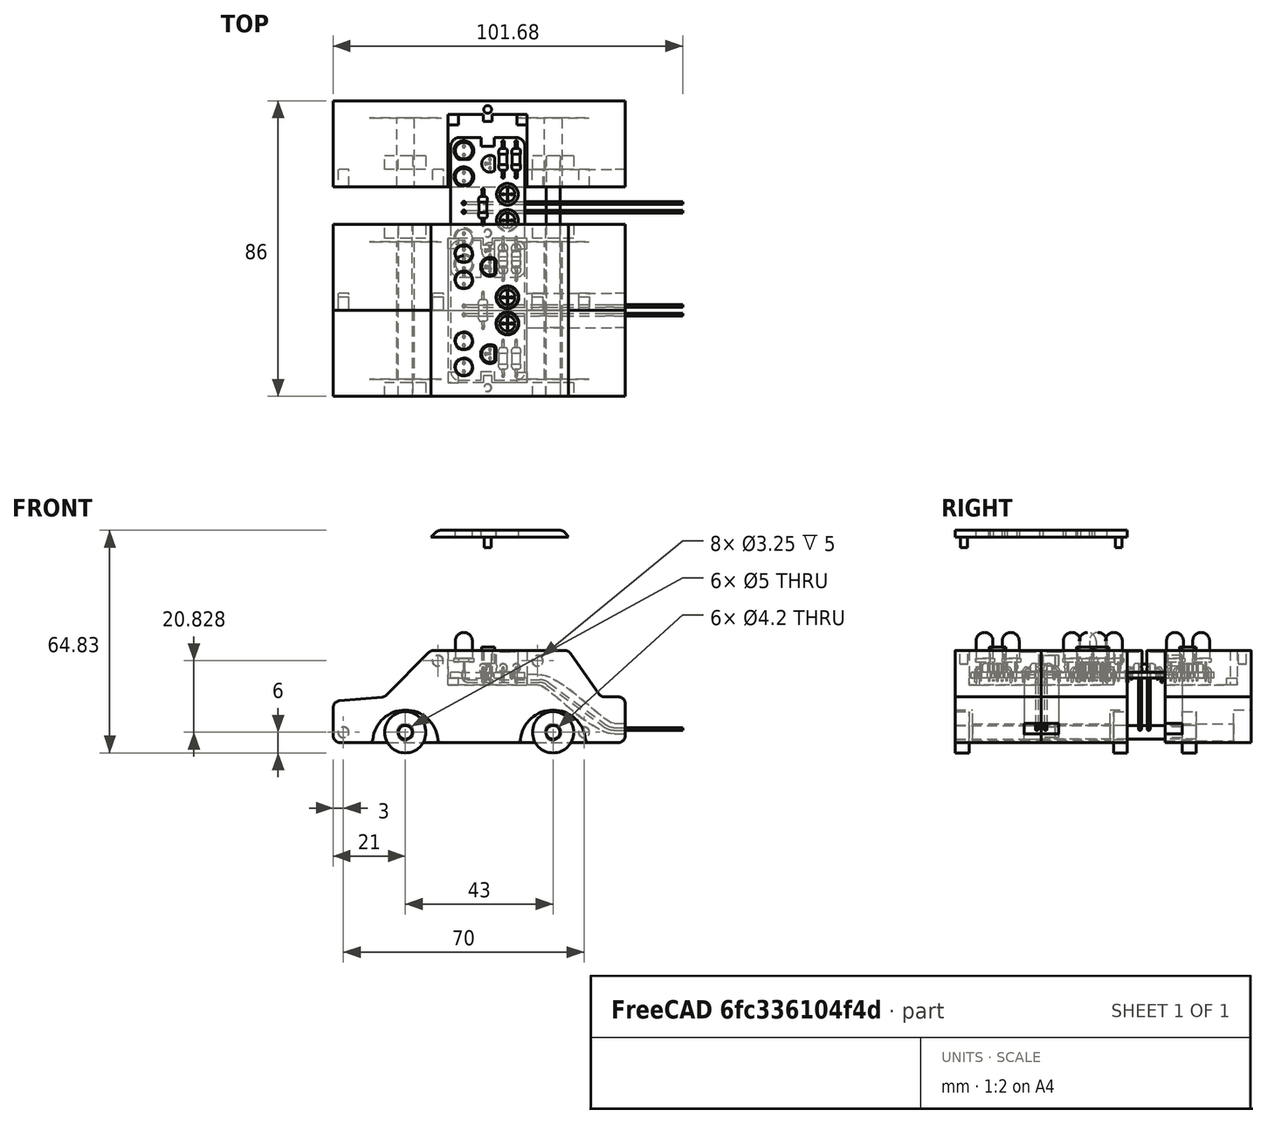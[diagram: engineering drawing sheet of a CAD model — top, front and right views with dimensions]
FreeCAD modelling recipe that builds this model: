
FCSTD DOCUMENT  (FreeCAD 0.21R30029 (Git))
Label: Assembly
License: All rights reserved
LicenseURL: http://en.wikipedia.org/wiki/All_rights_reserved
objects: PartDesign::FeatureBase×26, PartDesign::Body×26, TechDraw::DrawViewPart×13, Part::FeaturePython×10, App::DocumentObjectGroup×6, App::Part×2, TechDraw::DrawSVGTemplate×1, TechDraw::DrawPage×1
note: 62 computed .brp shape members not serialized (recipe doc carries the construction recipe); baked Part::Feature solids carry a one-line shape summary decoded from their .brp

FEATURE [Part::FeaturePython] b_PCB1_001_  label="PCB1_001"  # a2plus imported part (geometry in sourceFile) (typed FeaturePython)
  Placement = pos=(45.5,-0.49,18.8275) rot=(0,0,1;1.5708rad)
  a2p_Version = V0.1
  fixedPosition = true
  objectType = a2pPart
  sourceFile = PCB_w_Wire.FCStd
  subassemblyImport = false
  timeLastImport = 1.66233e+09
  updateColors = true
FEATURE [Part::FeaturePython] b_LightTop_001_  label="LightTop_001"  # a2plus imported part (geometry in sourceFile) (typed FeaturePython)
  Placement = pos=(28.46,0,26.83) rot=(0,0,1;0rad)
  a2p_Version = V0.1
  fixedPosition = false
  objectType = a2pPart
  sourceFile = ./LightTop.FCStd
  subassemblyImport = false
  timeLastImport = 1.66241e+09
  updateColors = true
FEATURE [Part::FeaturePython] b_Car_001_  label="Car_Body001_001"  # a2plus imported part (geometry in sourceFile) (typed FeaturePython)
  a2p_Version = V0.1
  fixedPosition = false
  objectType = a2pPart
  sourceFile = ./Car.FCStd
  sourcePart = Body001
  subassemblyImport = false
  timeLastImport = 1.66233e+09
  updateColors = true
FEATURE [Part::FeaturePython] b_Car_001_001  label="Car_Body002_001"  # a2plus imported part (geometry in sourceFile) (typed FeaturePython)
  a2p_Version = V0.1
  fixedPosition = false
  objectType = a2pPart
  sourceFile = ./Car.FCStd
  sourcePart = Body002
  subassemblyImport = false
  timeLastImport = 1.66233e+09
  updateColors = true
FEATURE [Part::FeaturePython] b_Car_001_002  label="Car_Body003_001"  # a2plus imported part (geometry in sourceFile) (typed FeaturePython)
  a2p_Version = V0.1
  fixedPosition = false
  objectType = a2pPart
  sourceFile = ./Car.FCStd
  sourcePart = Body003
  subassemblyImport = false
  timeLastImport = 1.66233e+09
  updateColors = true
FEATURE [Part::FeaturePython] b_Car_001_003  label="Car_Body004_001"  # a2plus imported part (geometry in sourceFile) (typed FeaturePython)
  a2p_Version = V0.1
  fixedPosition = false
  objectType = a2pPart
  sourceFile = ./Car.FCStd
  sourcePart = Body004
  subassemblyImport = false
  timeLastImport = 1.66233e+09
  updateColors = true
FEATURE [Part::FeaturePython] b_Car_Body002_001_  label="Car_Body002_002"  # a2plus imported part (geometry in sourceFile) (typed FeaturePython)
  Placement = pos=(0,46,0) rot=(0,0,1;0rad)
  a2p_Version = V0.1
  fixedPosition = false
  objectType = a2pPart
  sourceFile = ./Car.FCStd
  sourcePart = Body002
  subassemblyImport = false
  timeLastImport = 1.66233e+09
  updateColors = true
FEATURE [Part::FeaturePython] b_Car_Body002_001_001  label="Car_Body002_003"  # a2plus imported part (geometry in sourceFile) (typed FeaturePython)
  Placement = pos=(43,46,0) rot=(0,0,1;0rad)
  a2p_Version = V0.1
  fixedPosition = false
  objectType = a2pPart
  sourceFile = ./Car.FCStd
  sourcePart = Body002
  subassemblyImport = false
  timeLastImport = 1.66233e+09
  updateColors = true
FEATURE [Part::FeaturePython] b_Car_Body002_001_002  label="Car_Body002_004"  # a2plus imported part (geometry in sourceFile) (typed FeaturePython)
  Placement = pos=(43,0,0) rot=(0,0,1;0rad)
  a2p_Version = V0.1
  fixedPosition = false
  objectType = a2pPart
  sourceFile = ./Car.FCStd
  sourcePart = Body002
  subassemblyImport = false
  timeLastImport = 1.66233e+09
  updateColors = true
FEATURE [Part::FeaturePython] b_Car_Body001_001_  label="Car_Body001_002"  # a2plus imported part (geometry in sourceFile) (typed FeaturePython)
  Placement = pos=(43,0,0) rot=(0,0,1;0rad)
  a2p_Version = V0.1
  fixedPosition = false
  objectType = a2pPart
  sourceFile = ./Car.FCStd
  sourcePart = Body001
  subassemblyImport = false
  timeLastImport = 1.66233e+09
  updateColors = true
FEATURE [App::DocumentObjectGroup] Group  label="Full Assembly"
  Group = -> [b_Car_Body001_001_,b_Car_Body002_001_002,b_Car_001_003,b_Car_Body002_001_001,b_Car_001_002,b_Car_001_001,b_Car_001_,b_LightTop_001_,b_Car_Body002_001_,b_PCB1_001_]
FEATURE [PartDesign::FeatureBase] Clone
  BaseFeature = -> b_Car_001_003
FEATURE [PartDesign::Body] Body
  BaseFeature = -> b_Car_001_003
  Group = -> [Clone]
  Origin = -> Origin
  Tip = -> Clone
FEATURE [PartDesign::FeatureBase] Clone001
  BaseFeature = -> b_PCB1_001_
  Placement = pos=(45.5,-0.49,18.8275) rot=(0,0,1;1.5708rad)
FEATURE [PartDesign::Body] Body001
  BaseFeature = -> b_PCB1_001_
  Group = -> [Clone001]
  Origin = -> Origin001
  Placement = pos=(0,30,0) rot=(0,0,1;0rad)
  Tip = -> Clone001
FEATURE [App::DocumentObjectGroup] Group001  label="Step 1"
  Group = -> [Body,Body001]
FEATURE [PartDesign::FeatureBase] Clone002
  BaseFeature = -> b_PCB1_001_
  Placement = pos=(45.5,-0.49,18.8275) rot=(0,0,1;1.5708rad)
FEATURE [PartDesign::Body] Body002
  BaseFeature = -> b_PCB1_001_
  Group = -> [Clone002]
  Origin = -> Origin002
  Tip = -> Clone002
FEATURE [PartDesign::FeatureBase] Clone003
  BaseFeature = -> b_Car_001_003
FEATURE [PartDesign::Body] Body003
  BaseFeature = -> b_Car_001_003
  Group = -> [Clone003]
  Origin = -> Origin003
  Tip = -> Clone003
FEATURE [PartDesign::FeatureBase] Clone004
  BaseFeature = -> b_Car_001_002
FEATURE [PartDesign::Body] Body004
  BaseFeature = -> b_Car_001_002
  Group = -> [Clone004]
  Origin = -> Origin004
  Placement = pos=(0,36,0) rot=(0,0,1;0rad)
  Tip = -> Clone004
FEATURE [App::DocumentObjectGroup] Group002  label="Step 2"
  Group = -> [Body002,Body003,Body004]
FEATURE [PartDesign::FeatureBase] Clone005
  BaseFeature = -> b_Car_Body002_001_002
  Placement = pos=(43,0,0) rot=(0,0,1;0rad)
FEATURE [PartDesign::Body] Body005
  BaseFeature = -> b_Car_Body002_001_002
  Group = -> [Clone005]
  Origin = -> Origin005
  Tip = -> Clone005
FEATURE [PartDesign::FeatureBase] Clone006
  BaseFeature = -> b_Car_Body001_001_
  Placement = pos=(43,0,0) rot=(0,0,1;0rad)
FEATURE [PartDesign::Body] Body006
  BaseFeature = -> b_Car_Body001_001_
  Group = -> [Clone006]
  Origin = -> Origin006
  Placement = pos=(0,20,0) rot=(0,0,1;0rad)
  Tip = -> Clone006
FEATURE [App::DocumentObjectGroup] Group003  label="Step 3"
  Group = -> [Body005,Body006]
FEATURE [PartDesign::FeatureBase] Clone007
  BaseFeature = -> b_Car_001_003
FEATURE [PartDesign::Body] Body007
  BaseFeature = -> b_Car_001_003
  Group = -> [Clone007]
  Origin = -> Origin007
  Tip = -> Clone007
FEATURE [PartDesign::FeatureBase] Clone008
  BaseFeature = -> b_Car_Body002_001_001
  Placement = pos=(43,46,0) rot=(0,0,1;0rad)
FEATURE [PartDesign::Body] Body008
  BaseFeature = -> b_Car_Body002_001_001
  Group = -> [Clone008]
  Origin = -> Origin008
  Placement = pos=(0,20,0) rot=(0,0,1;0rad)
  Tip = -> Clone008
FEATURE [PartDesign::FeatureBase] Clone009
  BaseFeature = -> b_Car_001_002
FEATURE [PartDesign::Body] Body009
  BaseFeature = -> b_Car_001_002
  Group = -> [Clone009]
  Origin = -> Origin009
  Tip = -> Clone009
FEATURE [PartDesign::FeatureBase] Clone010
  BaseFeature = -> b_Car_001_001
FEATURE [PartDesign::Body] Body010
  BaseFeature = -> b_Car_001_001
  Group = -> [Clone010]
  Origin = -> Origin010
  Tip = -> Clone010
FEATURE [PartDesign::FeatureBase] Clone011
  BaseFeature = -> b_Car_001_
FEATURE [PartDesign::Body] Body011
  BaseFeature = -> b_Car_001_
  Group = -> [Clone011]
  Origin = -> Origin011
  Tip = -> Clone011
FEATURE [PartDesign::FeatureBase] Clone012
  BaseFeature = -> b_PCB1_001_
  Placement = pos=(45.5,-0.49,18.8275) rot=(0,0,1;1.5708rad)
FEATURE [PartDesign::Body] Body012
  BaseFeature = -> b_PCB1_001_
  Group = -> [Clone012]
  Origin = -> Origin012
  Tip = -> Clone012
FEATURE [PartDesign::FeatureBase] Clone013
  BaseFeature = -> b_Car_Body002_001_
  Placement = pos=(0,46,0) rot=(0,0,1;0rad)
FEATURE [PartDesign::Body] Body013
  BaseFeature = -> b_Car_Body002_001_
  Group = -> [Clone013]
  Origin = -> Origin013
  Placement = pos=(0,20,0) rot=(0,0,1;0rad)
  Tip = -> Clone013
FEATURE [PartDesign::FeatureBase] Clone014
  BaseFeature = -> b_Car_Body001_001_
  Placement = pos=(43,0,0) rot=(0,0,1;0rad)
FEATURE [PartDesign::Body] Body014
  BaseFeature = -> b_Car_Body001_001_
  Group = -> [Clone014]
  Origin = -> Origin014
  Tip = -> Clone014
FEATURE [PartDesign::FeatureBase] Clone015
  BaseFeature = -> b_Car_Body002_001_002
  Placement = pos=(43,0,0) rot=(0,0,1;0rad)
FEATURE [PartDesign::Body] Body015
  BaseFeature = -> b_Car_Body002_001_002
  Group = -> [Clone015]
  Origin = -> Origin015
  Tip = -> Clone015
FEATURE [App::Part] Part
  Group = -> [Body014,Body015]
  Origin = -> Origin016
  Placement = pos=(0,-80,0) rot=(0,0,1;0rad)
FEATURE [App::Part] Part001
  Group = -> [Body010,Body011]
  Origin = -> Origin017
  Placement = pos=(0,-80,0) rot=(0,0,1;0rad)
FEATURE [App::DocumentObjectGroup] Group004  label="Step 4"
  Group = -> [Body007,Body008,Body009,Body012,Body013,Part,Part001]
FEATURE [PartDesign::FeatureBase] Clone016
  BaseFeature = -> b_Car_Body001_001_
  Placement = pos=(43,0,0) rot=(0,0,1;0rad)
FEATURE [PartDesign::Body] Body016
  BaseFeature = -> b_Car_Body001_001_
  Group = -> [Clone016]
  Origin = -> Origin018
  Tip = -> Clone016
FEATURE [PartDesign::FeatureBase] Clone017
  BaseFeature = -> b_Car_Body002_001_002
  Placement = pos=(43,0,0) rot=(0,0,1;0rad)
FEATURE [PartDesign::Body] Body017
  BaseFeature = -> b_Car_Body002_001_002
  Group = -> [Clone017]
  Origin = -> Origin019
  Tip = -> Clone017
FEATURE [PartDesign::FeatureBase] Clone018
  BaseFeature = -> b_Car_001_003
FEATURE [PartDesign::Body] Body018
  BaseFeature = -> b_Car_001_003
  Group = -> [Clone018]
  Origin = -> Origin020
  Tip = -> Clone018
FEATURE [PartDesign::FeatureBase] Clone019
  BaseFeature = -> b_Car_Body002_001_001
  Placement = pos=(43,46,0) rot=(0,0,1;0rad)
FEATURE [PartDesign::Body] Body019
  BaseFeature = -> b_Car_Body002_001_001
  Group = -> [Clone019]
  Origin = -> Origin021
  Tip = -> Clone019
FEATURE [PartDesign::FeatureBase] Clone020
  BaseFeature = -> b_Car_001_002
FEATURE [PartDesign::Body] Body020
  BaseFeature = -> b_Car_001_002
  Group = -> [Clone020]
  Origin = -> Origin022
  Tip = -> Clone020
FEATURE [PartDesign::FeatureBase] Clone021
  BaseFeature = -> b_Car_001_001
FEATURE [PartDesign::Body] Body021
  BaseFeature = -> b_Car_001_001
  Group = -> [Clone021]
  Origin = -> Origin023
  Tip = -> Clone021
FEATURE [PartDesign::FeatureBase] Clone022
  BaseFeature = -> b_Car_001_
FEATURE [PartDesign::Body] Body022
  BaseFeature = -> b_Car_001_
  Group = -> [Clone022]
  Origin = -> Origin024
  Tip = -> Clone022
FEATURE [PartDesign::FeatureBase] Clone023
  BaseFeature = -> b_LightTop_001_
  Placement = pos=(28.46,0,26.83) rot=(0,0,1;0rad)
FEATURE [PartDesign::Body] Body023
  BaseFeature = -> b_LightTop_001_
  Group = -> [Clone023]
  Origin = -> Origin025
  Placement = pos=(0,0,33) rot=(0,0,1;0rad)
  Tip = -> Clone023
FEATURE [PartDesign::FeatureBase] Clone024
  BaseFeature = -> b_Car_Body002_001_
  Placement = pos=(0,46,0) rot=(0,0,1;0rad)
FEATURE [PartDesign::Body] Body024
  BaseFeature = -> b_Car_Body002_001_
  Group = -> [Clone024]
  Origin = -> Origin026
  Tip = -> Clone024
FEATURE [PartDesign::FeatureBase] Clone025
  BaseFeature = -> b_PCB1_001_
  Placement = pos=(45.5,-0.49,18.8275) rot=(0,0,1;1.5708rad)
FEATURE [PartDesign::Body] Body025
  BaseFeature = -> b_PCB1_001_
  Group = -> [Clone025]
  Origin = -> Origin027
  Tip = -> Clone025
FEATURE [App::DocumentObjectGroup] Group005  label="Step 5"
  Group = -> [Body016,Body017,Body018,Body019,Body020,Body021,Body022,Body023,Body024,Body025]
FEATURE [TechDraw::DrawSVGTemplate] Template
  Height = 297
  Orientation = 1
  Width = 420
FEATURE [TechDraw::DrawViewPart] View
  CoarseView = false
  Direction = (0.577,0.577,0.577)
  Focus = 100
  HardHidden = false
  IsoCount = 0
  IsoHidden = false
  IsoVisible = false
  LockPosition = false
  Perspective = false
  Rotation = 0
  ScaleType = 0
  SeamHidden = false
  SeamVisible = true
  SmoothHidden = false
  SmoothVisible = true
  Source = -> [Group001]
  X = 51.7341
  XDirection = (-0.707,0.707,0)
  Y = 248.907
FEATURE [TechDraw::DrawViewPart] View001
  CoarseView = false
  Direction = (0.577,0.577,0.577)
  Focus = 100
  HardHidden = false
  IsoCount = 0
  IsoHidden = false
  IsoVisible = false
  LockPosition = false
  Perspective = false
  Rotation = 0
  ScaleType = 0
  SeamHidden = false
  SeamVisible = true
  SmoothHidden = false
  SmoothVisible = true
  Source = -> [Group002]
  X = 164.35
  XDirection = (-0.707,0.707,0)
  Y = 248.729
FEATURE [TechDraw::DrawViewPart] View002
  CoarseView = false
  Direction = (0.577,0.577,0.577)
  Focus = 100
  HardHidden = false
  IsoCount = 0
  IsoHidden = false
  IsoVisible = false
  LockPosition = false
  Perspective = false
  Rotation = 0
  ScaleType = 0
  SeamHidden = false
  SeamVisible = true
  SmoothHidden = false
  SmoothVisible = true
  Source = -> [Group003]
  X = 43.8926
  XDirection = (-0.707,0.707,0)
  Y = 174.818
FEATURE [TechDraw::DrawViewPart] View003
  CoarseView = false
  Direction = (0.577,0.577,0.577)
  Focus = 100
  HardHidden = false
  IsoCount = 0
  IsoHidden = false
  IsoVisible = false
  LockPosition = false
  Perspective = false
  Rotation = 0
  ScaleType = 0
  SeamHidden = false
  SeamVisible = true
  SmoothHidden = false
  SmoothVisible = true
  Source = -> [Group004]
  X = 305.04
  XDirection = (-0.707,0.707,0)
  Y = 244.838
FEATURE [TechDraw::DrawViewPart] View004
  CoarseView = false
  Direction = (0.577,0.577,0.577)
  Focus = 100
  HardHidden = false
  IsoCount = 0
  IsoHidden = false
  IsoVisible = false
  LockPosition = false
  Perspective = false
  Rotation = 0
  ScaleType = 0
  SeamHidden = false
  SeamVisible = true
  SmoothHidden = false
  SmoothVisible = true
  Source = -> [Group005]
  X = 127.796
  XDirection = (-0.707,0.707,0)
  Y = 148.208
FEATURE [TechDraw::DrawViewPart] View005
  CoarseView = false
  Direction = (0.577,0.577,0.577)
  Focus = 100
  HardHidden = false
  IsoCount = 0
  IsoHidden = false
  IsoVisible = false
  LockPosition = false
  Perspective = false
  Rotation = 0
  ScaleType = 0
  SeamHidden = false
  SeamVisible = true
  SmoothHidden = false
  SmoothVisible = true
  Source = -> [Group]
  X = 234.017
  XDirection = (-0.707,0.707,0)
  Y = 150.854
FEATURE [TechDraw::DrawViewPart] View006
  CoarseView = false
  Direction = (0.577,0.577,0.577)
  Focus = 100
  HardHidden = false
  IsoCount = 0
  IsoHidden = false
  IsoVisible = false
  LockPosition = false
  Perspective = false
  Rotation = 0
  ScaleType = 0
  SeamHidden = false
  SeamVisible = true
  SmoothHidden = false
  SmoothVisible = true
  Source = -> [b_Car_Body001_001_]
  X = 315.916
  XDirection = (-0.707,0.707,0)
  Y = 170.664
FEATURE [TechDraw::DrawViewPart] View007
  CoarseView = false
  Direction = (0.577,0.577,0.577)
  Focus = 100
  HardHidden = false
  IsoCount = 0
  IsoHidden = false
  IsoVisible = false
  LockPosition = false
  Perspective = false
  Rotation = 0
  ScaleType = 0
  SeamHidden = false
  SeamVisible = true
  SmoothHidden = false
  SmoothVisible = true
  Source = -> [b_Car_001_003]
  X = 194.02
  XDirection = (-0.707,0.707,0)
  Y = 55.063
FEATURE [TechDraw::DrawViewPart] View008
  CoarseView = false
  Direction = (0.577,0.577,0.577)
  Focus = 100
  HardHidden = false
  IsoCount = 0
  IsoHidden = false
  IsoVisible = false
  LockPosition = false
  Perspective = false
  Rotation = 0
  ScaleType = 0
  SeamHidden = false
  SeamVisible = true
  SmoothHidden = false
  SmoothVisible = true
  Source = -> [b_Car_Body002_001_001]
  X = 119.67
  XDirection = (-0.707,0.707,0)
  Y = 44.4098
FEATURE [TechDraw::DrawViewPart] View009
  CoarseView = false
  Direction = (0.577,0.577,0.577)
  Focus = 100
  HardHidden = false
  IsoCount = 0
  IsoHidden = false
  IsoVisible = false
  LockPosition = false
  Perspective = false
  Rotation = 0
  ScaleType = 0
  SeamHidden = false
  SeamVisible = true
  SmoothHidden = false
  SmoothVisible = true
  Source = -> [b_Car_001_002]
  X = 295.447
  XDirection = (-0.707,0.707,0)
  Y = 62.1651
FEATURE [TechDraw::DrawViewPart] View010
  CoarseView = false
  Direction = (0.577,0.577,0.577)
  Focus = 100
  HardHidden = false
  IsoCount = 0
  IsoHidden = false
  IsoVisible = false
  LockPosition = false
  Perspective = false
  Rotation = 0
  ScaleType = 0
  SeamHidden = false
  SeamVisible = true
  SmoothHidden = false
  SmoothVisible = true
  Source = -> [b_LightTop_001_]
  X = 377.335
  XDirection = (-0.707,0.707,0)
  Y = 89.1601
FEATURE [TechDraw::DrawViewPart] View011
  CoarseView = false
  Direction = (0.577,0.577,0.577)
  Focus = 100
  HardHidden = false
  IsoCount = 0
  IsoHidden = false
  IsoVisible = false
  LockPosition = false
  Perspective = false
  Rotation = 0
  ScaleType = 0
  SeamHidden = false
  SeamVisible = true
  SmoothHidden = false
  SmoothVisible = true
  Source = -> [b_PCB1_001_]
  X = 377.007
  XDirection = (-0.707,0.707,0)
  Y = 152.862
FEATURE [TechDraw::DrawViewPart] View012
  CoarseView = false
  Direction = (0.577,-0.577,0.577)
  Focus = 100
  HardHidden = false
  IsoCount = 0
  IsoHidden = false
  IsoVisible = false
  LockPosition = false
  Perspective = false
  Rotation = 0
  ScaleType = 0
  SeamHidden = false
  SeamVisible = true
  SmoothHidden = false
  SmoothVisible = true
  Source = -> [b_Car_001_002]
  X = 50.7053
  XDirection = (0.707,0.707,0)
  Y = 53.2733
FEATURE [TechDraw::DrawPage] Page
  KeepUpdated = true
  NextBalloonIndex = 1
  ProjectionType = 0
  Template = -> Template
  Views = -> [View,View001,View002,View003,View004,View005,View006,View007,View008,View009,View010,View011,View012]
